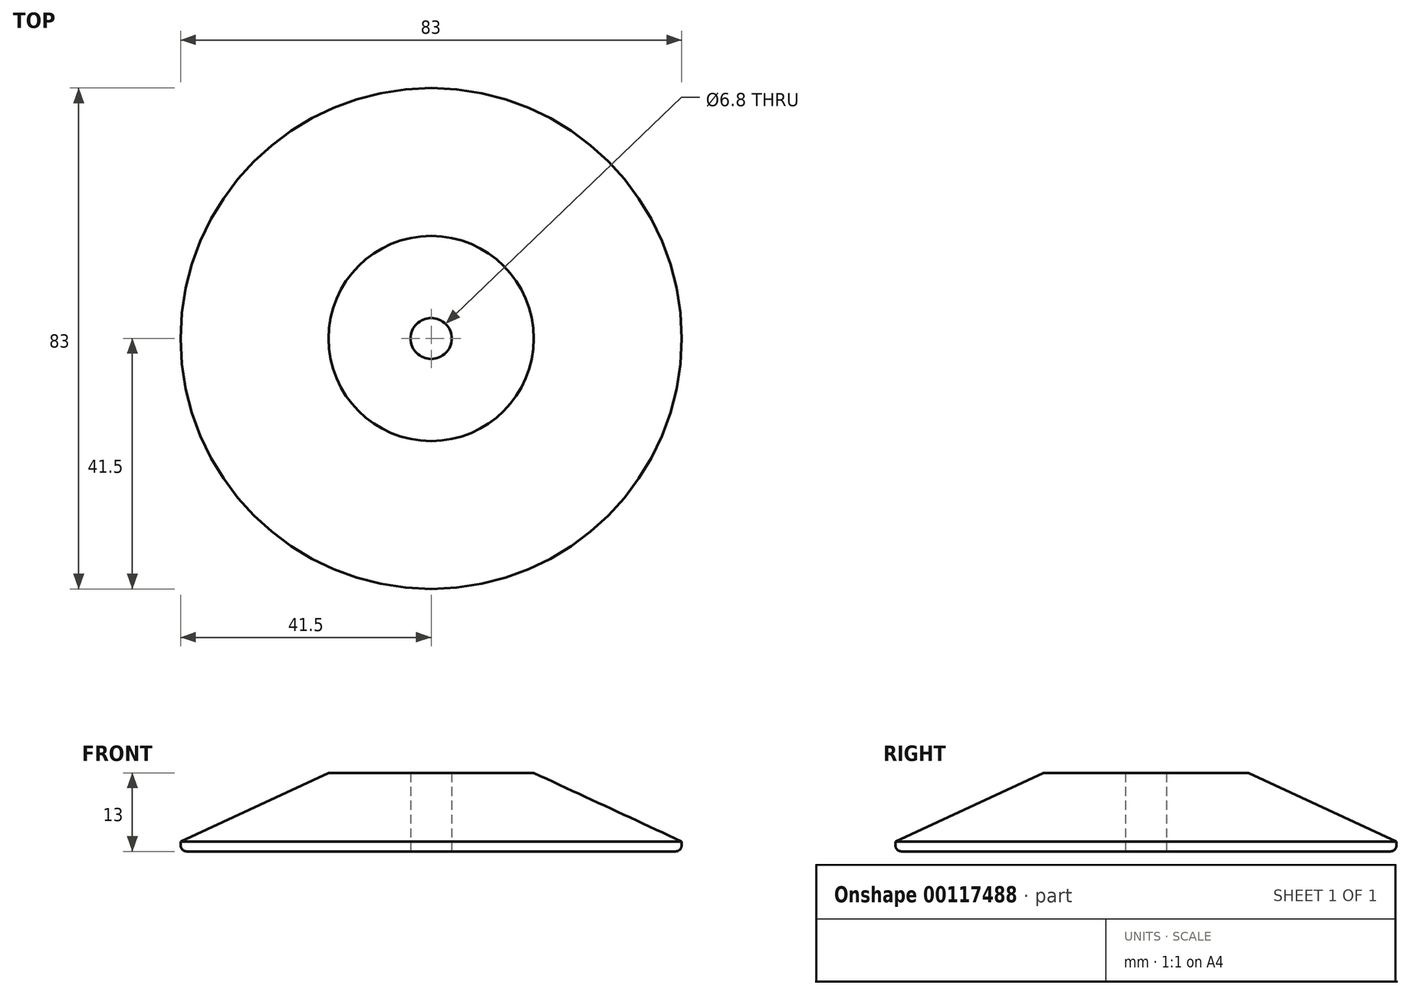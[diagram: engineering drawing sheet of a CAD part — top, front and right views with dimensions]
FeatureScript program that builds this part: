
annotation { "Feature Type Name" : "Feature", "Feature Type Description" : "" }
export const myFeature = defineFeature(function(context is Context, id is Id, definition is map)
    precondition{}
    {
        {
            var Q0;
            Q0=qCreatedBy(makeId("Right.planeOp"),FACE);
            var sketch = newSketch(context, id + "F0", { "sketchPlane" : qUnion([Q0])});
            skLineSegment(sketch, "E0", {"start": v(41.5, 1) * mm, "end": v(41.5, 1.65) * mm});
            skLineSegment(sketch, "E1", {"start": v(41.5, 1.65) * mm, "end": v(17, 13) * mm});
            skLineSegment(sketch, "E2", {"start": v(17, 13) * mm, "end": v(0, 13) * mm});
            skLineSegment(sketch, "E3", {"start": v(0, 13) * mm, "end": v(0, 0) * mm});
            skLineSegment(sketch, "E4", {"start": v(0, 0) * mm, "end": v(40.5, 0) * mm});
            skPoint(sketch, "E5.visualSharp", {"position": v(41.5, 0) * mm});
            skArc(sketch, "E5.filletArc", {"start": v(40.5, 0) * mm, "mid": v(41.2, 0.3) * mm, "end": v(41.5, 1) * mm});
            skSolve(sketch);
        }
        {
            var Q0;
            Q0=makeQuery(id+"F0.imprint","IMPRINT",FACE,{"disambiguationData":[TD([[makeQuery(id+"F0.imprint","IMPRINT",EDGE,{"derivedFrom":sQuery(id+"F0.wireOp",EDGE,"E0")}),1.0]])]});
            var Q1;
            Q1=sQuery(id+"F0.wireOp",EDGE,"E3");
            revolve(context, id + "F1", {"entities" : qUnion([Q0]), "axis" : qUnion([Q1]), "revolveType" : RevolveType.FULL});
        }
        {
            var Q0;
            Q0=qCreatedBy(makeId("Top.planeOp"),FACE);
            var sketch = newSketch(context, id + "F2", { "sketchPlane" : qUnion([Q0])});
            skPoint(sketch, "E6", {"position": v(0, 0) * mm});
            skSolve(sketch);
        }
        {
            var Q0;
            Q0=sQuery(id+"F2.wireOp",VERTEX,"E6");
            var Q1;
            Q1=makeQuery(id+"F1.opRevolve","SWEPT_BODY",BODY,{"disambiguationData":[OSD([sQuery(id+"F0.wireOp",EDGE,"E0"),sQuery(id+"F0.wireOp",EDGE,"E1"),sQuery(id+"F0.wireOp",EDGE,"E2"),sQuery(id+"F0.wireOp",EDGE,"E3"),sQuery(id+"F0.wireOp",EDGE,"E4"),sQuery(id+"F0.wireOp",EDGE,"E5.filletArc")])]});
            hole(context, id + "F3", {"style" : HoleStyle.SIMPLE, "endStyle" : HoleEndStyle.THROUGH, "oppositeDirection" : true, "standardTappedOrClearance" : lookupTablePath({ "standard" : "ISO", "engagement" : "75%", "pitch" : "1.25 mm", "size" : "M8", "type" : "Tapped" }), "standardBlindInLast" : lookupTablePath({ "standard" : "ISO", "engagement" : "75%", "pitch" : "1.25 mm", "size" : "M8", "type" : "Tapped" }), "holeDiameter" : 6.8 * mm, "locations" : qUnion([Q0]), "scope" : qUnion([Q1]), "isTappedThrough" : true, "majorDiameter" : 8 * mm, "showTappedDepth" : true});
        }
    });
